# Revit family: SVTC15-50
name_source: partatom
category: Mechanical Equipment
revit_build: Autodesk Revit 2013 (Build: 20130531_2115(x64)
units: mm (PartAtom-declared; Revit-internal decimal feet)

## types (4) — shared parameters
Catalogue Pages = http://www.nuaire.info
Description = Car Park Impulse Fan
Electrical Phase = 3
Fax Number = +44(0)2920-858-222
Height = 227 mm
I&M Manual = http://www.nuaire.info
Length = 1265 mm
Manufacturer = Nuaire
Manufacturer Name = Nuaire
Postcode = CF83 1NA
Telephone Number = +44(0)2920-858-200
URL = http://www.nuaire.co.uk
Unit Description = Car Park Impulse Fan
VAT Registration Number = 877308
Voltage = 400 V
Warranty Period = 3 Years
Weatherproof or Internal Only = Internal
Width = 790 mm

## per-type parameters (varying)
| type | Apparent Load | Full Load Current | Model | Nominal Motor Rating | Nominal Motor Speed (rpm) | Nuaire Model Code | Number of Connection Poles | Number of Motor Poles | Revit Family Last Revised | Starting Current | Weight |
| SVTC-15 | 1320 VA | 3 A | SVCT-15 | 1500 W | 1435 | SVCT-15 | 3 | 4 |  | 6 A | 130.00 kg |
| SVTC-15T6 | 1440 VA | 4 A | SVCT-15T6 | 1500 W | 1425 | SVCT-15T6 | 1 | 6 |  | 7 A | 130.00 kg |
| SVTC-15T8 | 1500 VA | 4 A | SVCT-15T8 | 1500 W | 1430 | SVCT-15T8 | 1 | 8 | 05/10/16 | 5 A | 130.00 kg |
| SVTC-50 | 6540 VA | 16 A | SVCT-50 | 1100 W | 1435 | SVCT-50 | 1 | 4 |  | 3 A | 100.00 kg |

## geometry (parser evidence)
native form markers: Blend x2, Sweep x9
no freeform markers — native parametric forms only
